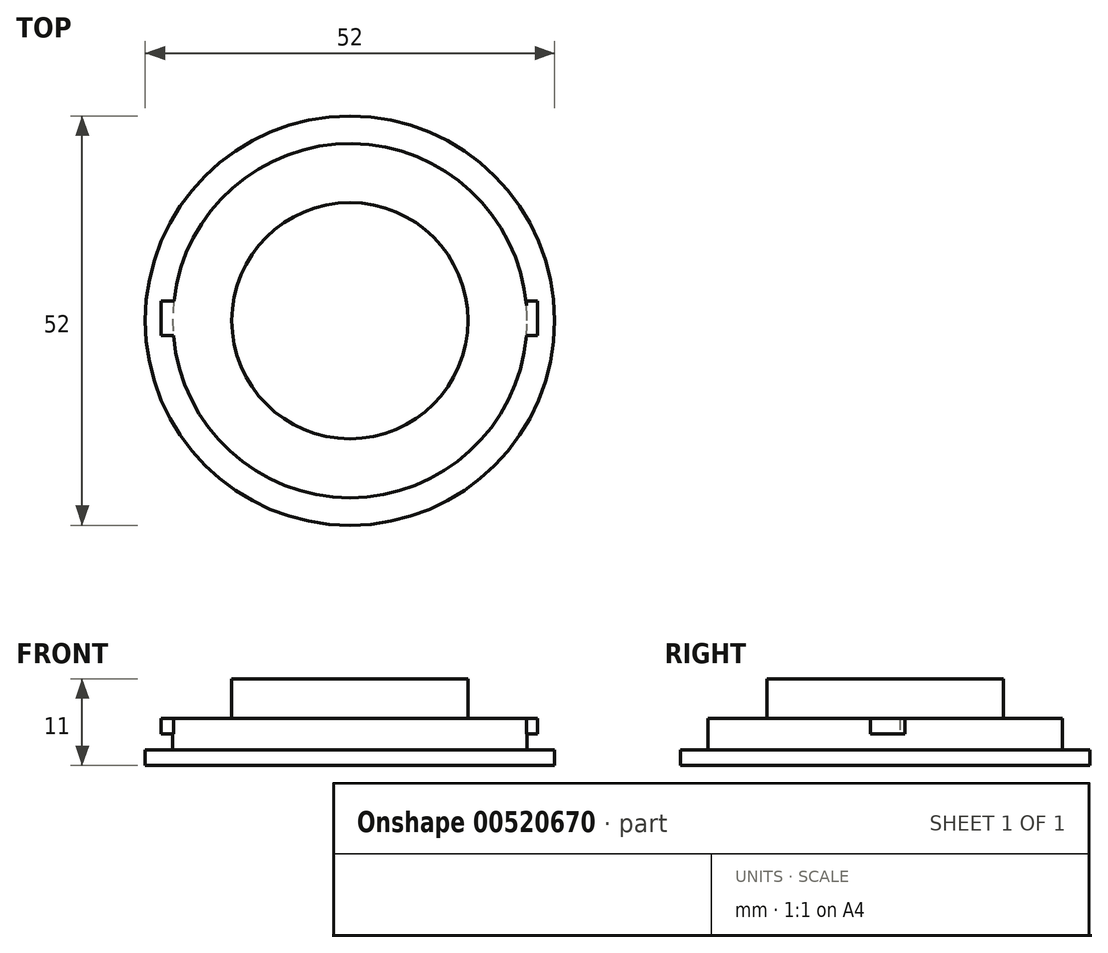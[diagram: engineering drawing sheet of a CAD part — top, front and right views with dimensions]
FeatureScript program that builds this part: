
annotation { "Feature Type Name" : "Feature", "Feature Type Description" : "" }
export const myFeature = defineFeature(function(context is Context, id is Id, definition is map)
    precondition{}
    {
        {
            var Q0;
            Q0=qCreatedBy(makeId("Top.planeOp"),FACE);
            var sketch = newSketch(context, id + "F0", { "sketchPlane" : qUnion([Q0])});
            skCircle(sketch, "E0", {"center": v(0, 0) * mm, "radius": 26 * mm});
            skSolve(sketch);
        }
        {
            var Q0;
            Q0 = qSketchRegion(id + "F0", true);
            extrude(context, id + "F1", {"entities" : qUnion([Q0]), "depth" : 2 * mm, "offsetDistance" : 25 * mm});
        }
        {
            var Q0;
            Q0=makeQuery(id+"F1.opExtrude","CAP_FACE",FACE,{"disambiguationData":[OSD([sQuery(id+"F0.wireOp",EDGE,"E0")])],"isStart":false});
            var sketch = newSketch(context, id + "F2", { "sketchPlane" : qUnion([Q0])});
            skCircle(sketch, "E1", {"center": v(0, 0) * mm, "radius": 22.5 * mm});
            skSolve(sketch);
        }
        {
            var Q0;
            Q0 = qSketchRegion(id + "F2", true);
            extrude(context, id + "F3", {"entities" : qUnion([Q0]), "operationType" : NewBodyOperationType.ADD, "depth" : 2 * mm, "offsetDistance" : 25 * mm});
        }
        {
            var Q0;
            Q0=makeQuery(id+"F3.opExtrude","CAP_FACE",FACE,{"disambiguationData":[OSD([sQuery(id+"F2.wireOp",EDGE,"E1")])],"isStart":false});
            var sketch = newSketch(context, id + "F4", { "sketchPlane" : qUnion([Q0])});
            skLineSegment(sketch, "E2.bottom", {"start": v(-22.35, 2.5) * mm, "end": v(-24.01, 2.5) * mm});
            skLineSegment(sketch, "E2.top", {"start": v(-22.35, -1.9) * mm, "end": v(-24.01, -1.9) * mm});
            skLineSegment(sketch, "E2.left", {"start": v(-22.35, 2.5) * mm, "end": v(-22.35, -1.9) * mm});
            skLineSegment(sketch, "E2.right", {"start": v(-24.01, 2.5) * mm, "end": v(-24.01, -1.9) * mm});
            skLineSegment(sketch, "E3.bottom", {"start": v(23.84, 2.5) * mm, "end": v(22.42, 2.5) * mm});
            skLineSegment(sketch, "E3.top", {"start": v(23.84, -1.9) * mm, "end": v(22.42, -1.9) * mm});
            skLineSegment(sketch, "E3.left", {"start": v(23.84, 2.5) * mm, "end": v(23.84, -1.9) * mm});
            skLineSegment(sketch, "E3.right", {"start": v(22.42, 2.5) * mm, "end": v(22.42, -1.9) * mm});
            skCircle(sketch, "E4", {"center": v(0, 0) * mm, "radius": 22.5 * mm});
            skSolve(sketch);
        }
        {
            var Q0;
            Q0 = qSketchRegion(id + "F4", true);
            extrude(context, id + "F5", {"entities" : qUnion([Q0]), "operationType" : NewBodyOperationType.ADD, "depth" : 2 * mm, "offsetDistance" : 25 * mm});
        }
        {
            var Q0;
            Q0=makeQuery(id+"F5.opExtrude","CAP_FACE",FACE,{"disambiguationData":[OSD([sQuery(id+"F4.wireOp",EDGE,"E2.bottom"),sQuery(id+"F4.wireOp",EDGE,"E2.top"),sQuery(id+"F4.wireOp",EDGE,"E2.right"),sQuery(id+"F4.wireOp",EDGE,"E3.bottom"),sQuery(id+"F4.wireOp",EDGE,"E3.top"),sQuery(id+"F4.wireOp",EDGE,"E3.left"),sQuery(id+"F4.wireOp",EDGE,"E3.right"),sQuery(id+"F4.wireOp",EDGE,"E4")])],"isStart":false});
            var sketch = newSketch(context, id + "F6", { "sketchPlane" : qUnion([Q0])});
            skCircle(sketch, "E5", {"center": v(0, 0) * mm, "radius": 15 * mm});
            skSolve(sketch);
        }
        {
            var Q0;
            Q0 = qSketchRegion(id + "F6", true);
            extrude(context, id + "F7", {"entities" : qUnion([Q0]), "operationType" : NewBodyOperationType.ADD, "depth" : 5 * mm, "offsetDistance" : 25 * mm});
        }
    });
